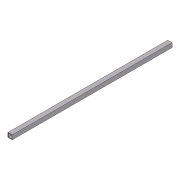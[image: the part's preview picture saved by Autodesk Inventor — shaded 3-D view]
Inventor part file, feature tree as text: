
AUTODESK INVENTOR PART (.ipt)
format: ipt  version: 2012 (Build 160160000, 160)  size: 71,168 bytes
history: native  units: in
note: dims shown in document units (in); Inventor stores cm internally (conversion verified against a paired STEP export)
features: extrude x1, shell x1, sketch x1
ambient origin geometry x8: Origin, YZ Plane, XZ Plane, XY Plane, X Axis, Y Axis, Z Axis, Center Point
bodies: Solid1 (feature_tree)
feature tree (3):
  extrude  "Extrusion1"  Depth=1.0in
  shell  "Shell1"  Thickness=37.0in
  sketch  "Sketch1"  dims[d0=1.0in d1=1.0in d2=37.0in d3=0.0in d4=0.125in]
